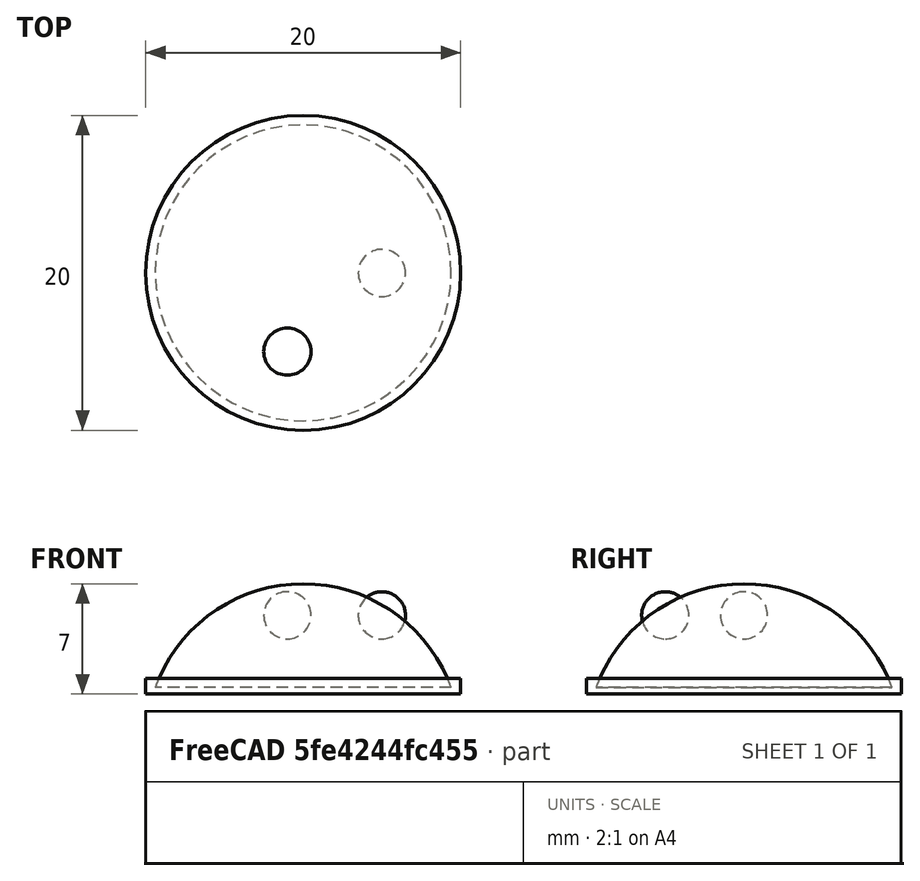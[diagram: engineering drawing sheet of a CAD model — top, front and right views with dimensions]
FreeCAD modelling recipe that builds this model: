
FCSTD DOCUMENT  (FreeCAD 0.21R33694 (Git))
Label: OJT1_T13R01_robot
License: All rights reserved
LicenseURL: http://en.wikipedia.org/wiki/All_rights_reserved
objects: Part::Sphere×3, Part::Cylinder×1
note: 4 computed .brp shape members not serialized (recipe doc carries the construction recipe); baked Part::Feature solids carry a one-line shape summary decoded from their .brp

FEATURE [Part::Cylinder] Cylinder  label="base"
  Angle = 360
  AttacherType = Attacher::AttachEngine3D
  FirstAngle = 0
  Height = 1
  Radius = 10
  SecondAngle = 0
FEATURE [Part::Sphere] Sphere  label="cap"
  Angle1 = 20
  Angle2 = 90
  Angle3 = 360
  AttacherType = Attacher::AttachEngine3D
  Placement = pos=(0,0,-3) rot=(0,0,1;0rad)
  Radius = 10
FEATURE [Part::Sphere] Sphere001  label="ull1"
  Angle1 = -90
  Angle2 = 90
  Angle3 = 360
  AttacherType = Attacher::AttachEngine3D
  Placement = pos=(5,0,5) rot=(0,0,1;0rad)
  Radius = 1.5
FEATURE [Part::Sphere] Sphere002  label="ull2"
  Angle1 = -90
  Angle2 = 90
  Angle3 = 360
  AttacherType = Attacher::AttachEngine3D
  Placement = pos=(-1,-5,5) rot=(0,0,1;0rad)
  Radius = 1.5
